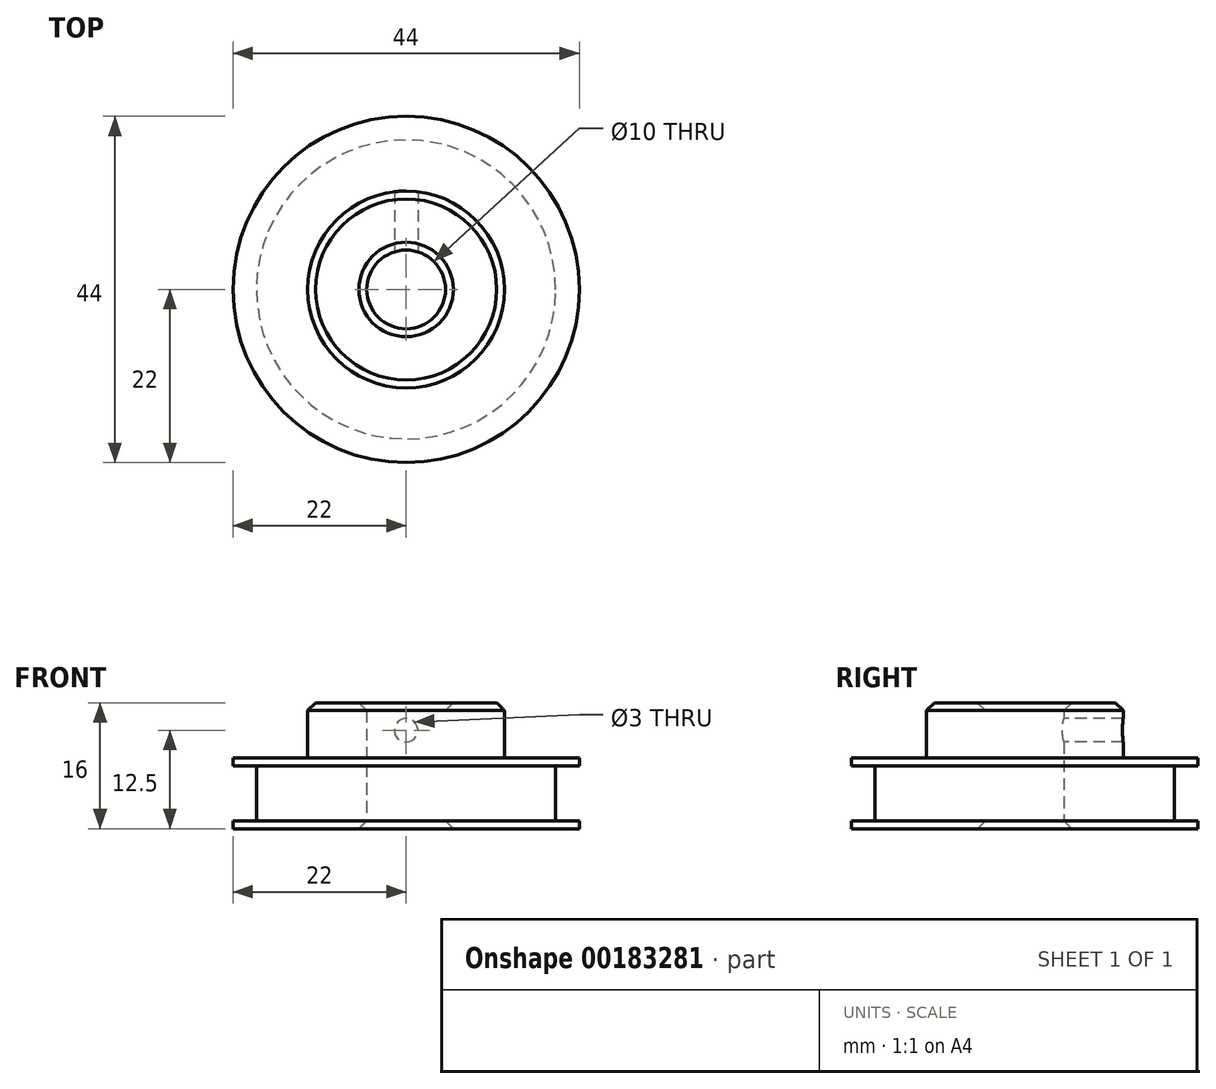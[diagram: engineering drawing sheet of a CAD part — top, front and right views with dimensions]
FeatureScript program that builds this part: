
annotation { "Feature Type Name" : "Feature", "Feature Type Description" : "" }
export const myFeature = defineFeature(function(context is Context, id is Id, definition is map)
    precondition{}
    {
        {
            var Q0;
            Q0=qCreatedBy(makeId("Top.planeOp"),FACE);
            var sketch = newSketch(context, id + "F0", { "sketchPlane" : qUnion([Q0])});
            skCircle(sketch, "E0", {"center": v(0, 0) * mm, "radius": 5 * mm});
            skCircle(sketch, "E1", {"center": v(0, 0) * mm, "radius": 19 * mm});
            skSolve(sketch);
        }
        {
            var Q0;
            Q0 = qSketchRegion(id + "F0", true);
            extrude(context, id + "F1", {"entities" : qUnion([Q0]), "endBound" : BoundingType.SYMMETRIC, "depth" : 7 * mm});
        }
        {
            var Q0;
            Q0=makeQuery(id+"F1.opExtrude","CAP_FACE",FACE,{"disambiguationData":[OSD([sQuery(id+"F0.wireOp",EDGE,"E0"),sQuery(id+"F0.wireOp",EDGE,"E1")])],"isStart":false});
            var sketch = newSketch(context, id + "F2", { "sketchPlane" : qUnion([Q0])});
            skCircle(sketch, "E2", {"center": v(0, 0) * mm, "radius": 22 * mm});
            skCircle(sketch, "E3.0", {"center": v(0, 0) * mm, "radius": 5 * mm});
            skSolve(sketch);
        }
        {
            var Q0;
            Q0 = qSketchRegion(id + "F2", true);
            extrude(context, id + "F3", {"entities" : qUnion([Q0]), "depth" : 1 * mm});
        }
        {
            var Q0;
            Q0=makeQuery(id+"F3.opExtrude","SWEPT_BODY",BODY,{"disambiguationData":[OSD([sQuery(id+"F2.wireOp",EDGE,"E2"),sQuery(id+"F2.wireOp",EDGE,"E3.0")])]});
            var Q1;
            Q1=qCreatedBy(makeId("Top.planeOp"),FACE);
            mirror(context, id + "F4", {"operationType" : NewBodyOperationType.ADD, "entities" : qUnion([Q0]), "mirrorPlane" : qUnion([Q1])});
        }
        {
            var Q0;
            Q0=makeQuery(id+"F3.opExtrude","CAP_FACE",FACE,{"disambiguationData":[OSD([sQuery(id+"F2.wireOp",EDGE,"E2"),sQuery(id+"F2.wireOp",EDGE,"E3.0")])],"isStart":false});
            var sketch = newSketch(context, id + "F5", { "sketchPlane" : qUnion([Q0])});
            skCircle(sketch, "E4", {"center": v(0, 0) * mm, "radius": 12.5 * mm});
            skCircle(sketch, "E5.0", {"center": v(0, 0) * mm, "radius": 5 * mm});
            skSolve(sketch);
        }
        {
            var Q0;
            Q0 = qSketchRegion(id + "F5", true);
            extrude(context, id + "F6", {"entities" : qUnion([Q0]), "operationType" : NewBodyOperationType.ADD, "depth" : 7 * mm});
        }
        {
            var Q0;
            Q0=makeQuery(id+"F6.opExtrude","CAP_EDGE",EDGE,{"disambiguationData":[OSD([sQuery(id+"F5.wireOp",EDGE,"E4")])],"isStart":false});
            var Q1;
            Q1=makeQuery(id+"F6.opExtrude","CAP_EDGE",EDGE,{"disambiguationData":[OSD([sQuery(id+"F5.wireOp",EDGE,"E5.0")])],"isStart":false});
            var Q2;
            Q2=makeQuery(id+"F4.opPattern","COPY",EDGE,{"derivedFrom":makeQuery(id+"F3.opExtrude","CAP_EDGE",EDGE,{"disambiguationData":[OSD([sQuery(id+"F2.wireOp",EDGE,"E3.0")])],"isStart":false}),"instanceName":"1"});
            chamfer(context, id + "F7", {"entities" : qUnion([Q0, Q1, Q2]), "width" : 1 * mm, "tangentPropagation" : true});
        }
        {
            var Q0;
            Q0=qCreatedBy(makeId("Front.planeOp"),FACE);
            var sketch = newSketch(context, id + "F8", { "sketchPlane" : qUnion([Q0])});
            skCircle(sketch, "E6", {"center": v(0, 8) * mm, "radius": 1.5 * mm});
            skLineSegment(sketch, "E7", {"start": v(0, 11.5) * mm, "end": v(0, 4.5) * mm, "construction": true});
            skSolve(sketch);
        }
        {
            var Q0;
            Q0 = qSketchRegion(id + "F8", true);
            extrude(context, id + "F9", {"entities" : qUnion([Q0]), "operationType" : NewBodyOperationType.REMOVE, "endBound" : BoundingType.THROUGH_ALL, "oppositeDirection" : true, "depth" : 25 * mm});
        }
    });
